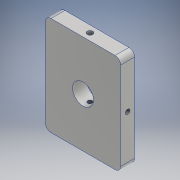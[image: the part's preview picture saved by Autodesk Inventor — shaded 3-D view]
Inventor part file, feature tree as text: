
AUTODESK INVENTOR PART (.ipt)
format: ipt  version: 2017 SP1 (Build 210196100, 196)  size: 143,360 bytes
history: native  units: mm
features: sketch x9, hole x6, extrude x2, fillet x1
ambient origin geometry x8: Origin, YZ Plane, XZ Plane, XY Plane, X Axis, Y Axis, Z Axis, Center Point
bodies: Body1 (feature_tree)
feature tree (18):
  extrude  "Extrusion4"  Depth=71.0mm
  extrude  "Extrusion5"  Depth=10.0mm
  hole  "Hole5"  [1 undecoded]
  sketch  "Sketch12"  dims[d46=3.242mm d47=8.0mm d48=4.0mm d49=2.0mm d50=90.0deg d51=11.8mm d52=20.594885mm]
  hole  "Hole6"  [1 undecoded]
  fillet  "Fillet3"  Radius=1.0mm
  sketch  "Sketch14"  dims[d61=4.0mm d62=8.0mm d63=4.0mm d64=2.0mm d65=90.0deg d66=20.0mm d67=0.0mm]
  hole  "Hole7"  [1 undecoded]
  hole  "Hole8"  [1 undecoded]
  sketch  "Sketch16"  dims[d75=3.242mm d76=8.0mm d77=4.0mm d78=2.0mm d79=90.0deg d80=11.8mm d81=0.0mm]
  hole  "Hole9"  [1 undecoded]
  hole  "Hole10"  [1 undecoded]
  sketch  "Sketch9"  dims[d39=54.0mm d40=71.0mm]
  sketch  "Sketch10"  dims[d41=10.0mm d42=0.0mm d43=15.0mm]
  sketch  "Sketch11"  dims[d44=10.0mm d45=0.0mm]
  sketch  "Sketch13"  dims[d53=2.459mm d54=6.0mm d55=4.0mm d56=2.0mm d57=90.0deg d58=8.8mm d59=20.594885mm d60=4.0mm]
  sketch  "Sketch15"  dims[d68=4.0mm d69=8.0mm d70=4.0mm d71=2.0mm d72=90.0deg d73=20.0mm d74=0.0mm]
  sketch  "Sketch17"  dims[d82=3.242mm d83=8.0mm d84=4.0mm d85=2.0mm d86=90.0deg d87=11.8mm d88=0.0mm d89=1.0mm d90=1.0mm]
note: 6 required parameter values undecoded (feature->parameter linkage not recoverable at this tier; creation-order binding heuristic only, values carry confidence <= 0.55)
